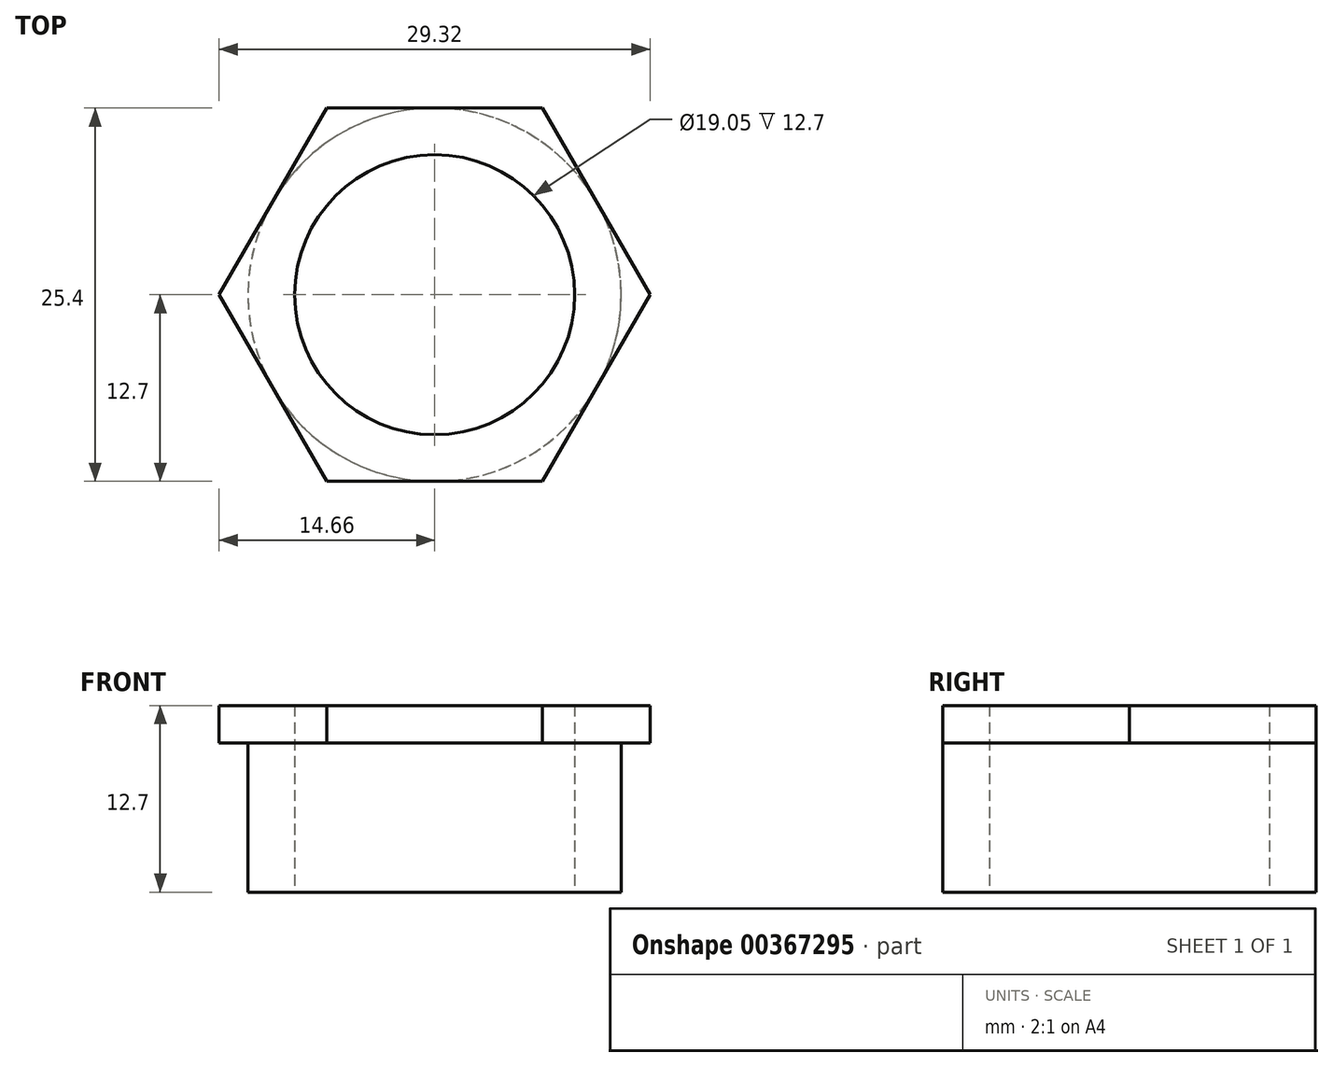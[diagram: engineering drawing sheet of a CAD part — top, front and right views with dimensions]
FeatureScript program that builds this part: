
annotation { "Feature Type Name" : "Feature", "Feature Type Description" : "" }
export const myFeature = defineFeature(function(context is Context, id is Id, definition is map)
    precondition{}
    {
        {
            var Q0;
            Q0=qCreatedBy(makeId("Top.planeOp"),FACE);
            var sketch = newSketch(context, id + "F0", { "sketchPlane" : qUnion([Q0])});
            skCircle(sketch, "E0", {"center": v(0, 0) * mm, "radius": 12.7 * mm});
            skCircle(sketch, "E1", {"center": v(0, 0) * mm, "radius": 9.53 * mm});
            skSolve(sketch);
        }
        {
            var Q0;
            Q0=qSketchRegion(id+"F0",true);
            extrude(context, id + "F1", {"entities" : qUnion([Q0]), "depth" : 12.7 * mm});
        }
        {
            var Q0;
            Q0=makeQuery(id+"F1.opExtrude","CAP_FACE",FACE,{"disambiguationData":[OSD([sQuery(id+"F0.wireOp",EDGE,"E0"),sQuery(id+"F0.wireOp",EDGE,"E1")])],"isStart":false});
            var sketch = newSketch(context, id + "F2", { "sketchPlane" : qUnion([Q0])});
            skCircle(sketch, "E2.cCircle", {"center": v(0, 0) * mm, "radius": 12.7 * mm, "construction": true});
            skLineSegment(sketch, "E2.0", {"start": v(-7.33, 12.7) * mm, "end": v(7.33, 12.7) * mm});
            skLineSegment(sketch, "E2.1", {"start": v(7.33, 12.7) * mm, "end": v(14.66, 0) * mm});
            skLineSegment(sketch, "E2.2", {"start": v(14.66, 0) * mm, "end": v(7.33, -12.7) * mm});
            skLineSegment(sketch, "E2.3", {"start": v(7.33, -12.7) * mm, "end": v(-7.33, -12.7) * mm});
            skLineSegment(sketch, "E2.4", {"start": v(-7.33, -12.7) * mm, "end": v(-14.66, 0) * mm});
            skLineSegment(sketch, "E2.5", {"start": v(-14.66, 0) * mm, "end": v(-7.33, 12.7) * mm});
            skPoint(sketch, "E2.0.midPoint", {"position": v(0, 12.7) * mm});
            skCircle(sketch, "E3", {"center": v(0, 0) * mm, "radius": 9.53 * mm});
            skSolve(sketch);
        }
        {
            var Q0;
            Q0=qSketchRegion(id+"F2",true);
            var Q1;
            Q1=qConstructionFilter(qBodyType(qCreatedBy(id+"F2",EDGE),BodyType.WIRE),ConstructionObject.NO);
            extrude(context, id + "F3", {"entities" : qUnion([Q0]), "operationType" : NewBodyOperationType.ADD, "surfaceEntities" : qUnion([Q1]), "oppositeDirection" : true, "depth" : 2.54 * mm});
        }
    });
